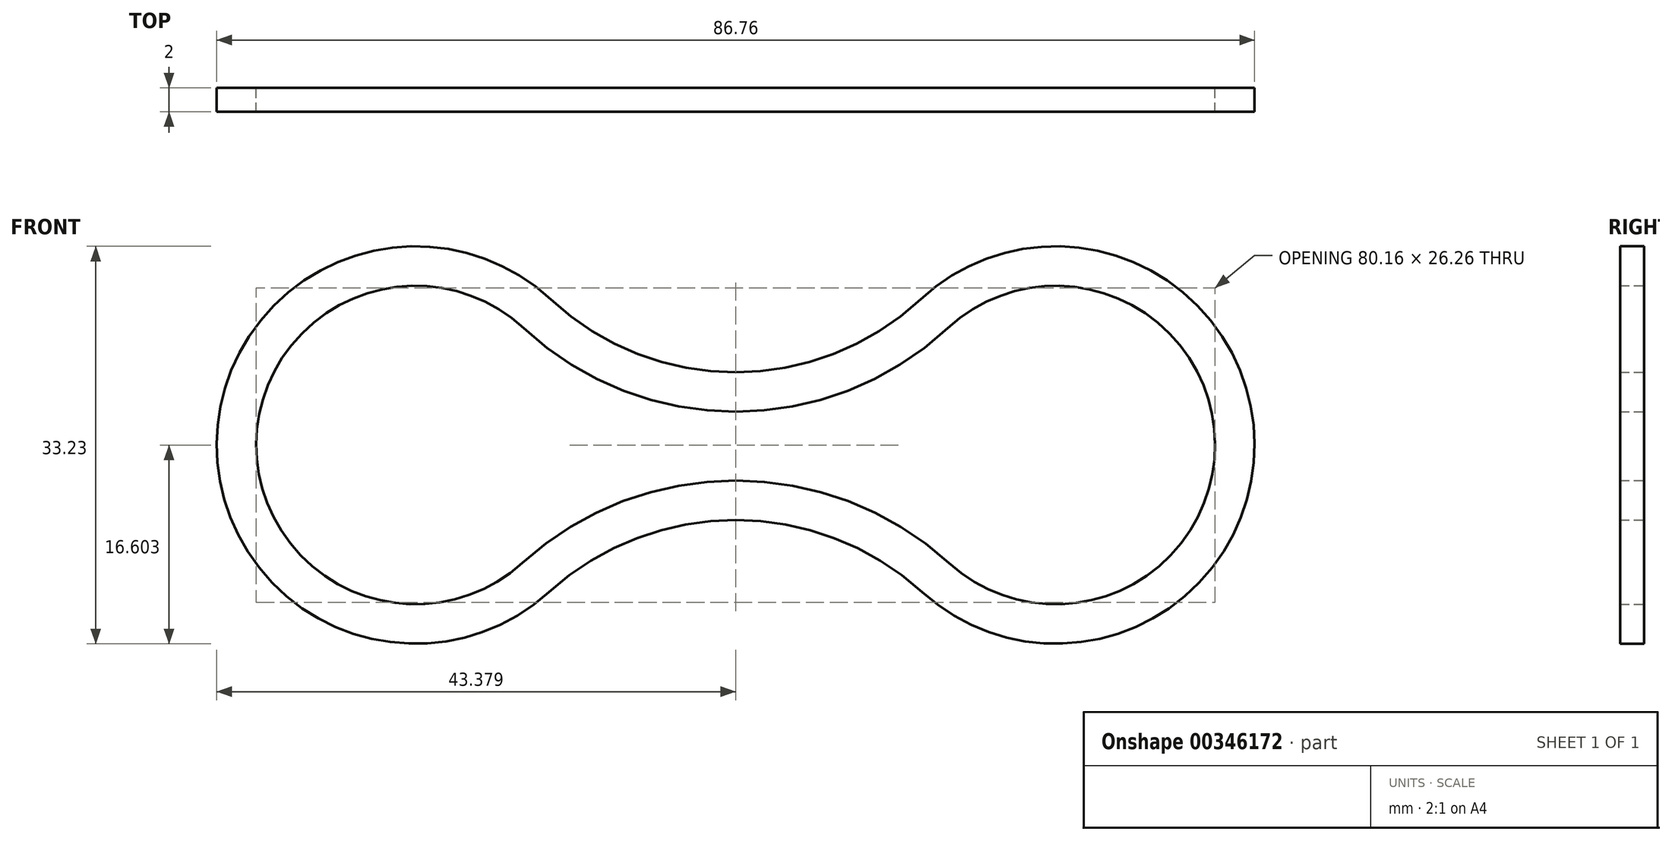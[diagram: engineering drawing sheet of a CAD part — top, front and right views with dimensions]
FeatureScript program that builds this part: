
annotation { "Feature Type Name" : "Feature", "Feature Type Description" : "" }
export const myFeature = defineFeature(function(context is Context, id is Id, definition is map)
    precondition{}
    {
        {
            var Q0;
            Q0=qCreatedBy(makeId("Front.planeOp"),FACE);
            var sketch = newSketch(context, id + "F0", { "sketchPlane" : qUnion([Q0])});
            skArc(sketch, "E0", {"start": v(-42.23, 25.02) * mm, "mid": v(-70.15, 12.95) * mm, "end": v(-42.38, 0.56) * mm});
            skArc(sketch, "E1", {"start": v(-11.17, 0.56) * mm, "mid": v(16.61, 12.95) * mm, "end": v(-11.3, 25.02) * mm});
            skArc(sketch, "E2", {"start": v(-11.17, 0.56) * mm, "mid": v(-26.77, 6.58) * mm, "end": v(-42.38, 0.56) * mm});
            skPoint(sketch, "E2.centerSnap0", {"position": v(-26.77, 12.86) * mm});
            skArc(sketch, "E3", {"start": v(-42.23, 25.02) * mm, "mid": v(-26.77, 18.95) * mm, "end": v(-11.3, 25.02) * mm});
            skArc(sketch, "E4.0", {"start": v(-44.48, 22.6) * mm, "mid": v(-26.77, 15.65) * mm, "end": v(-9.06, 22.6) * mm});
            skArc(sketch, "E4.1", {"start": v(-44.48, 22.6) * mm, "mid": v(-66.85, 12.93) * mm, "end": v(-44.6, 3) * mm});
            skArc(sketch, "E4.2", {"start": v(-8.95, 3) * mm, "mid": v(-26.77, 9.88) * mm, "end": v(-44.6, 3) * mm});
            skArc(sketch, "E4.3", {"start": v(-8.95, 3) * mm, "mid": v(13.31, 12.93) * mm, "end": v(-9.06, 22.6) * mm});
            skSolve(sketch);
        }
        {
            var Q0;
            Q0=makeQuery(id+"F0.imprint","IMPRINT",FACE,{"disambiguationData":[TD([[makeQuery(id+"F0.imprint","IMPRINT",EDGE,{"derivedFrom":sQuery(id+"F0.wireOp",EDGE,"E0")}),1.0]])]});
            extrude(context, id + "F1", {"entities" : qUnion([Q0]), "depth" : 2 * mm});
        }
    });
